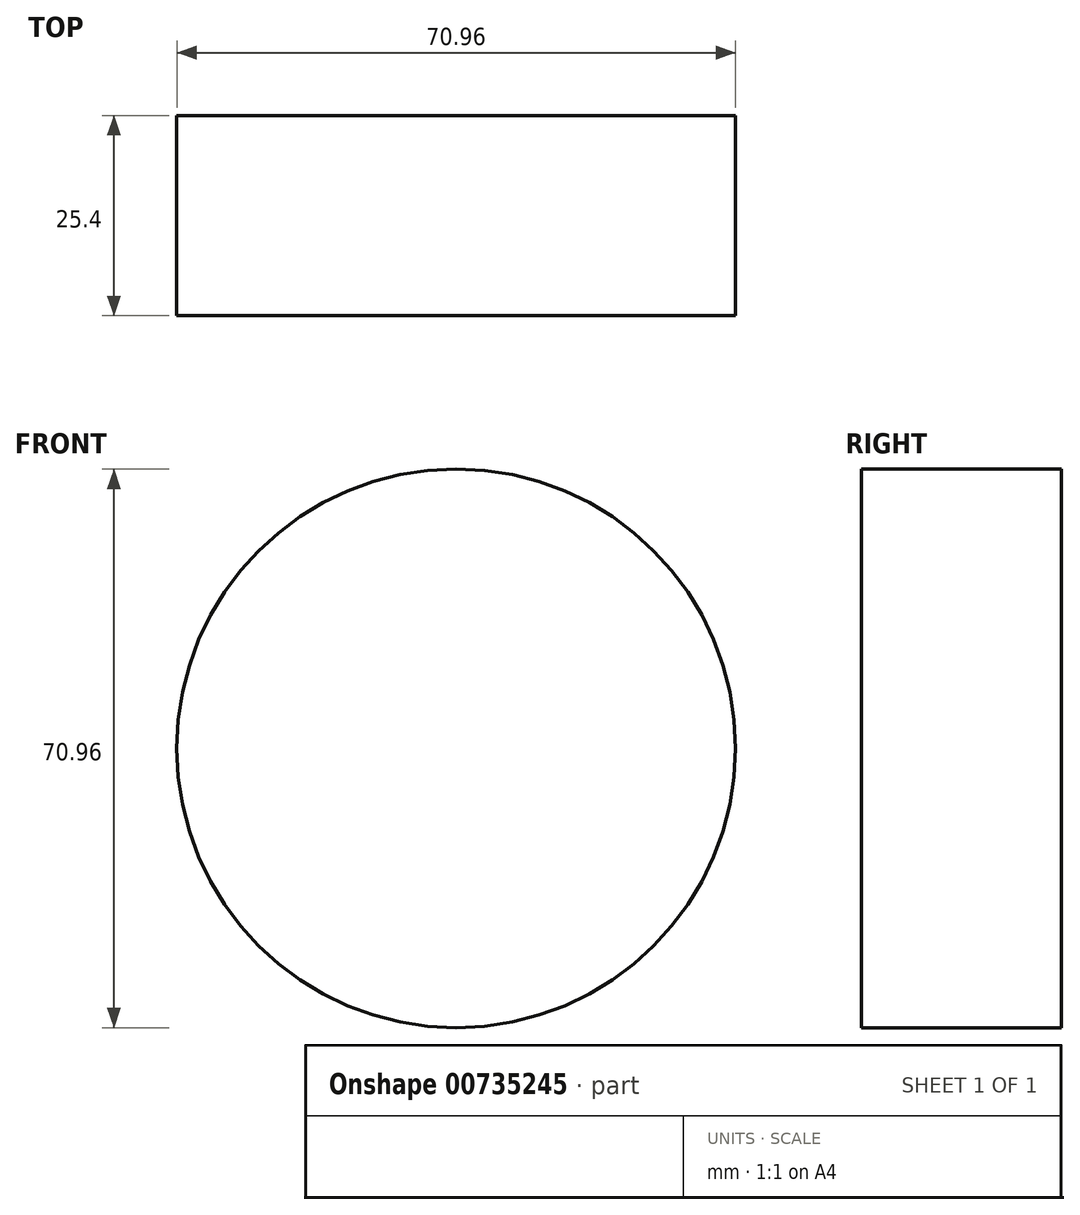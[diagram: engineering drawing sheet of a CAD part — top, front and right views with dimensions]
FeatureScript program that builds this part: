
annotation { "Feature Type Name" : "Feature", "Feature Type Description" : "" }
export const myFeature = defineFeature(function(context is Context, id is Id, definition is map)
    precondition{}
    {
        {
            var Q0;
            Q0=qCreatedBy(makeId("Front.planeOp"),FACE);
            var sketch = newSketch(context, id + "F0", { "sketchPlane" : qUnion([Q0])});
            skCircle(sketch, "E0", {"center": v(0, 0) * mm, "radius": 35.48 * mm});
            skSolve(sketch);
        }
        {
            var Q0;
            Q0 = qSketchRegion(id + "F0", true);
            extrude(context, id + "F1", {"entities" : qUnion([Q0]), "depth" : 25.4 * mm, "offsetDistance" : 25.4 * mm});
        }
    });
